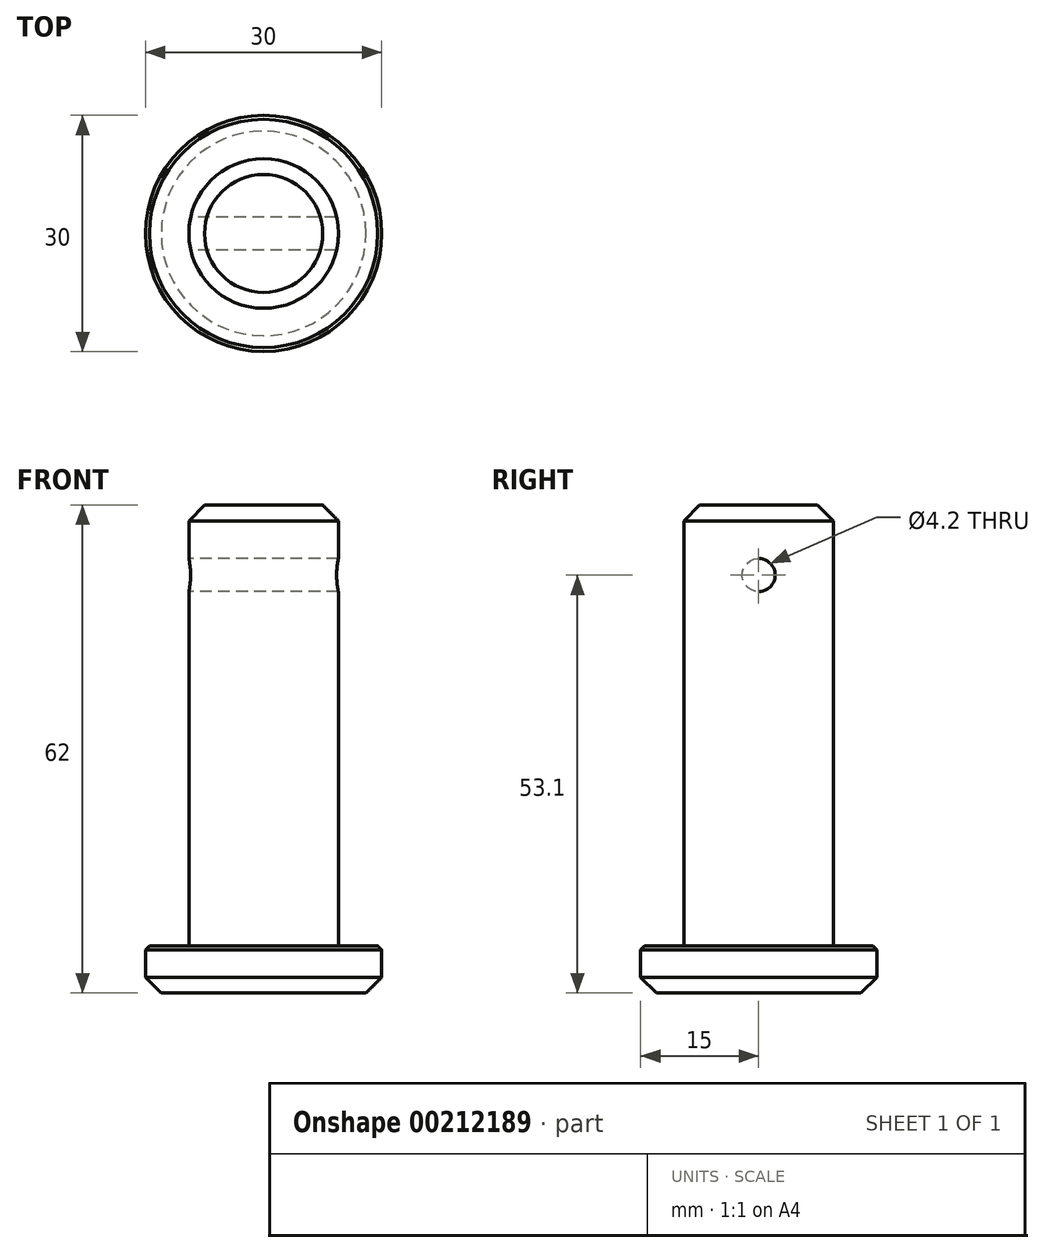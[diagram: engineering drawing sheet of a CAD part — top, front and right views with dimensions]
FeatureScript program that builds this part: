
annotation { "Feature Type Name" : "Feature", "Feature Type Description" : "" }
export const myFeature = defineFeature(function(context is Context, id is Id, definition is map)
    precondition{}
    {
        {
            var Q0;
            Q0=qCreatedBy(makeId("Top.planeOp"),FACE);
            var sketch = newSketch(context, id + "F0", { "sketchPlane" : qUnion([Q0])});
            skCircle(sketch, "E0", {"center": v(0, 0) * mm, "radius": 15 * mm});
            skCircle(sketch, "E1", {"center": v(0, 0) * mm, "radius": 9.5 * mm});
            skSolve(sketch);
        }
        {
            var Q0;
            Q0=makeQuery(id+"F0.imprint","IMPRINT",FACE,{"disambiguationData":[TD([[makeQuery(id+"F0.imprint","IMPRINT",EDGE,{"derivedFrom":sQuery(id+"F0.wireOp",EDGE,"E0")}),1.0]])]});
            extrude(context, id + "F1", {"entities" : qUnion([Q0]), "depth" : 6 * mm});
        }
        {
            var Q0;
            Q0=makeQuery(id+"F0.imprint","IMPRINT",FACE,{"disambiguationData":[TD([[makeQuery(id+"F0.imprint","IMPRINT",EDGE,{"derivedFrom":sQuery(id+"F0.wireOp",EDGE,"E1")}),1.0]])]});
            extrude(context, id + "F2", {"entities" : qUnion([Q0]), "operationType" : NewBodyOperationType.ADD, "depth" : 62 * mm});
        }
        {
            var Q0;
            Q0=qCreatedBy(makeId("Right.planeOp"),FACE);
            var sketch = newSketch(context, id + "F3", { "sketchPlane" : qUnion([Q0])});
            skCircle(sketch, "E2", {"center": v(0, 53.1) * mm, "radius": 2.1 * mm});
            skSolve(sketch);
        }
        {
            var Q0;
            Q0=sQuery(id+"F3.wireOp",VERTEX,"E2.center");
            var Q1;
            Q1=makeQuery(id+"F1.opExtrude","SWEPT_BODY",BODY,{"disambiguationData":[OSD([sQuery(id+"F0.wireOp",EDGE,"E0"),sQuery(id+"F0.wireOp",EDGE,"E1")])]});
            hole(context, id + "F4", {"style" : HoleStyle.SIMPLE, "endStyle" : HoleEndStyle.THROUGH, "oppositeDirection" : true, "standardTappedOrClearance" : lookupTablePath({ "standard" : "ISO", "size" : "4.2", "type" : "Drilled" }), "standardBlindInLast" : lookupTablePath({ "standard" : "ISO", "size" : "4.2", "type" : "Drilled" }), "holeDiameter" : 4.2 * mm, "locations" : qUnion([Q0]), "scope" : qUnion([Q1]), "tappedDepth" : 12 * mm, "tapClearance" : 3});
        }
        {
            var Q0;
            Q0=sQuery(id+"F3.wireOp",VERTEX,"E2.center");
            var Q1;
            Q1=makeQuery(id+"F1.opExtrude","SWEPT_BODY",BODY,{"disambiguationData":[OSD([sQuery(id+"F0.wireOp",EDGE,"E0"),sQuery(id+"F0.wireOp",EDGE,"E1")])]});
            hole(context, id + "F5", {"style" : HoleStyle.SIMPLE, "endStyle" : HoleEndStyle.THROUGH, "standardTappedOrClearance" : lookupTablePath({ "standard" : "ISO", "size" : "4.2", "type" : "Drilled" }), "standardBlindInLast" : lookupTablePath({ "standard" : "ISO", "size" : "4.2", "type" : "Drilled" }), "holeDiameter" : 4.2 * mm, "locations" : qUnion([Q0]), "scope" : qUnion([Q1]), "tappedDepth" : 12 * mm, "tapClearance" : 3});
        }
        {
            var Q0;
            Q0=makeQuery(id+"F2.opExtrude","CAP_EDGE",EDGE,{"disambiguationData":[OSD([sQuery(id+"F0.wireOp",EDGE,"E1")])],"isStart":false});
            var Q1;
            Q1=makeQuery(id+"F1.opExtrude","CAP_EDGE",EDGE,{"disambiguationData":[OSD([sQuery(id+"F0.wireOp",EDGE,"E0")])],"isStart":true});
            chamfer(context, id + "F6", {"entities" : qUnion([Q0, Q1]), "width" : 2 * mm, "tangentPropagation" : true});
        }
        {
            var Q0;
            Q0=makeQuery(id+"F5.hole-0.boolean.opBoolean","INTERSECT",EDGE,{"derivedFrom":[makeQuery(id+"F2.opExtrude","SWEPT_FACE",FACE,{"disambiguationData":[OSD([sQuery(id+"F0.wireOp",EDGE,"E1")])]}),makeQuery(id+"F5.hole-0.opRevolve","SWEPT_FACE",FACE,{"disambiguationData":[OSD([sQuery(id+"F5.hole-0.sketch.wireOp",EDGE,"core_line_2")])]})]});
            var Q1;
            Q1=makeQuery(id+"F4.hole-0.boolean.opBoolean","INTERSECT",EDGE,{"derivedFrom":[makeQuery(id+"F2.opExtrude","SWEPT_FACE",FACE,{"disambiguationData":[OSD([sQuery(id+"F0.wireOp",EDGE,"E1")])]}),makeQuery(id+"F4.hole-0.opRevolve","SWEPT_FACE",FACE,{"disambiguationData":[OSD([sQuery(id+"F4.hole-0.sketch.wireOp",EDGE,"core_line_2")])]})]});
            var Q2;
            Q2=makeQuery(id+"F1.opExtrude","CAP_EDGE",EDGE,{"disambiguationData":[OSD([sQuery(id+"F0.wireOp",EDGE,"E0")])],"isStart":false});
            chamfer(context, id + "F7", {"entities" : qUnion([Q0, Q1, Q2]), "width" : .5 * mm, "tangentPropagation" : true});
        }
    });
